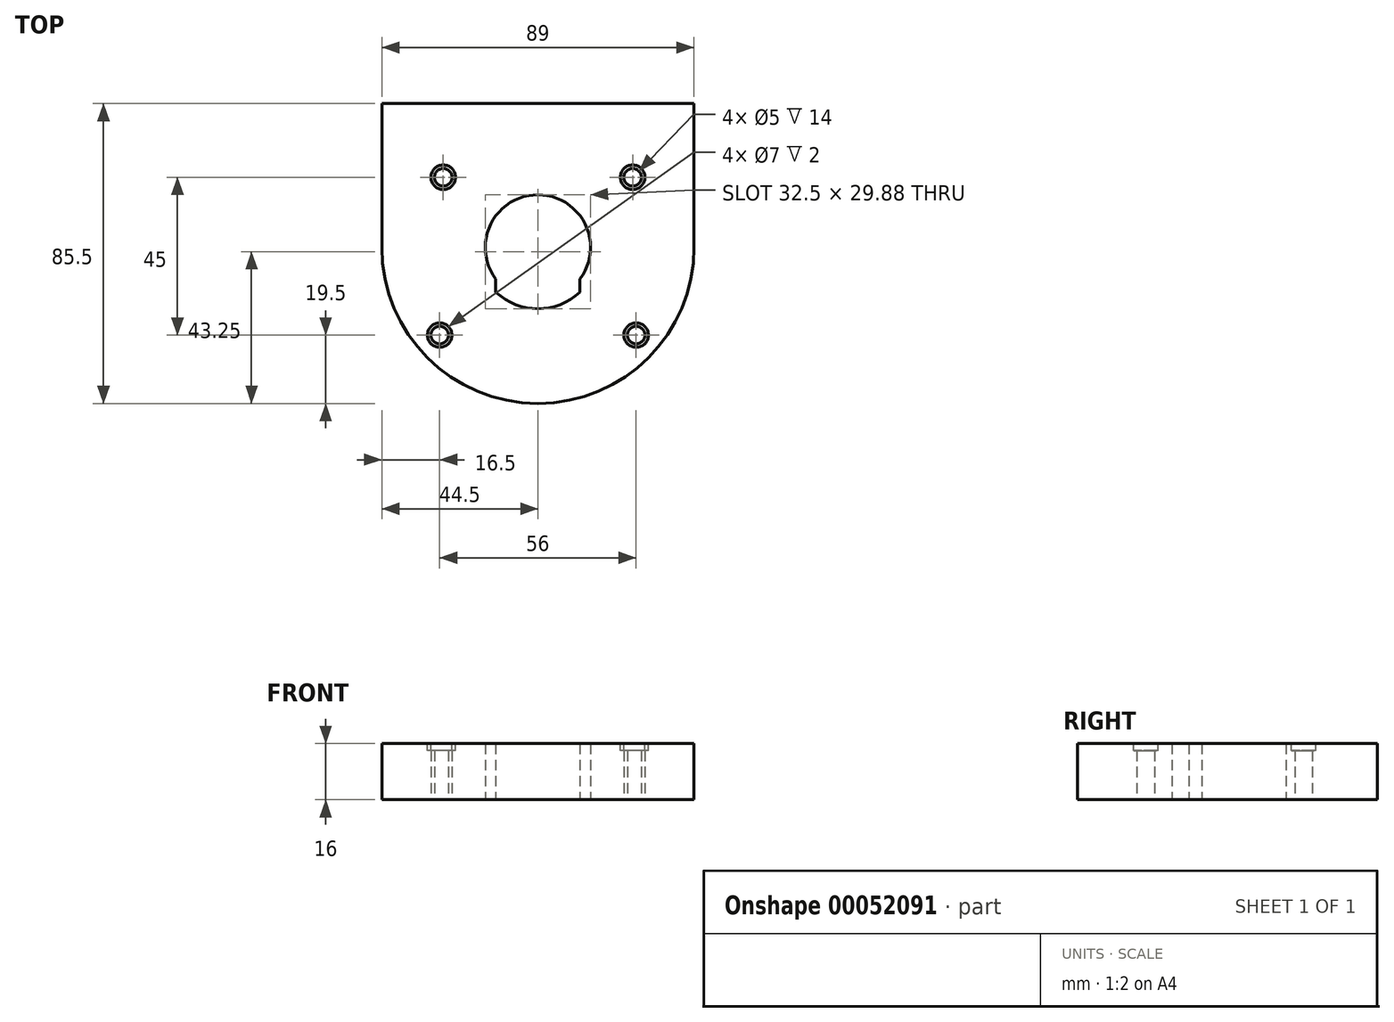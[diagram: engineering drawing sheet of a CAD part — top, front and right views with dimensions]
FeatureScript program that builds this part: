
annotation { "Feature Type Name" : "Feature", "Feature Type Description" : "" }
export const myFeature = defineFeature(function(context is Context, id is Id, definition is map)
    precondition{}
    {
        {
            var Q0;
            Q0=qCreatedBy(makeId("Top.planeOp"),FACE);
            var sketch = newSketch(context, id + "F0", { "sketchPlane" : qUnion([Q0])});
            skLineSegment(sketch, "E0", {"start": v(-44.5, 41) * mm, "end": v(44.5, 41) * mm});
            skCircle(sketch, "E1", {"center": v(-27, 20) * mm, "radius": 2.5 * mm});
            skCircle(sketch, "E2", {"center": v(27, 20) * mm, "radius": 2.5 * mm});
            skLineSegment(sketch, "E3", {"start": v(-44.5, 0) * mm, "end": v(-44.5, 41) * mm});
            skLineSegment(sketch, "E4", {"start": v(44.5, 0) * mm, "end": v(44.5, 41) * mm});
            skArc(sketch, "E5", {"start": v(12, -9) * mm, "mid": v(0, 15) * mm, "end": v(-12, -9) * mm});
            skArc(sketch, "E6", {"start": v(-12, -12.74) * mm, "mid": v(0, -17.5) * mm, "end": v(12, -12.74) * mm});
            skLineSegment(sketch, "E7", {"start": v(12, -12.74) * mm, "end": v(12, -9) * mm});
            skLineSegment(sketch, "E8.MirrorCS", {"start": v(-12, -12.74) * mm, "end": v(-12, -9) * mm});
            skCircle(sketch, "E9", {"center": v(-28, -25) * mm, "radius": 2.5 * mm});
            skCircle(sketch, "E10", {"center": v(28, -25) * mm, "radius": 2.5 * mm});
            skArc(sketch, "E11.trimOffspring", {"start": v(-44.5, 0) * mm, "mid": v(0, -44.5) * mm, "end": v(44.5, 0) * mm});
            skSolve(sketch);
        }
        {
            var Q0;
            Q0=makeQuery(id+"F0.imprint","IMPRINT",FACE,{"disambiguationData":[TD([[makeQuery(id+"F0.imprint","IMPRINT",EDGE,{"derivedFrom":sQuery(id+"F0.wireOp",EDGE,"E0")}),-1.0]])]});
            extrude(context, id + "F1", {"entities" : qUnion([Q0]), "depth" : 16 * mm});
        }
        {
            var Q0;
            Q0=makeQuery(id+"F1.opExtrude","CAP_FACE",FACE,{"disambiguationData":[OSD([sQuery(id+"F0.wireOp",EDGE,"E0"),sQuery(id+"F0.wireOp",EDGE,"E1"),sQuery(id+"F0.wireOp",EDGE,"E2"),sQuery(id+"F0.wireOp",EDGE,"E3"),sQuery(id+"F0.wireOp",EDGE,"E4"),sQuery(id+"F0.wireOp",EDGE,"E5"),sQuery(id+"F0.wireOp",EDGE,"E6"),sQuery(id+"F0.wireOp",EDGE,"E7"),sQuery(id+"F0.wireOp",EDGE,"E8.MirrorCS"),sQuery(id+"F0.wireOp",EDGE,"E9"),sQuery(id+"F0.wireOp",EDGE,"E10"),sQuery(id+"F0.wireOp",EDGE,"E11.trimOffspring")])],"isStart":false});
            var sketch = newSketch(context, id + "F2", { "sketchPlane" : qUnion([Q0])});
            skCircle(sketch, "E12", {"center": v(-27, 20) * mm, "radius": 3.5 * mm});
            skCircle(sketch, "E13", {"center": v(-28, -25) * mm, "radius": 3.5 * mm});
            skCircle(sketch, "E14.MirrorC", {"center": v(27, 20) * mm, "radius": 3.5 * mm});
            skCircle(sketch, "E15.MirrorC", {"center": v(28, -25) * mm, "radius": 3.5 * mm});
            skSolve(sketch);
        }
        {
            var Q0;
            Q0 = qSketchRegion(id + "F2", true);
            extrude(context, id + "F3", {"entities" : qUnion([Q0]), "operationType" : NewBodyOperationType.REMOVE, "oppositeDirection" : true, "depth" : 2 * mm});
        }
    });
